annotation { "Feature Type Name" : "Feature", "Feature Type Description" : "" }
export const myFeature = defineFeature(function(context is Context, id is Id, definition is map)
    precondition{}
    {
        {
            var Q0;
            Q0=qCreatedBy(makeId("Top.planeOp"),FACE);
            var sketch = newSketch(context, id + "F0", { "sketchPlane" : qUnion([Q0])});
            skLineSegment(sketch, "E0.bottom", {"start": v(-25, 46.27) * mm, "end": v(25, 46.27) * mm});
            skLineSegment(sketch, "E0.top", {"start": v(-25, -46.27) * mm, "end": v(25, -46.27) * mm});
            skLineSegment(sketch, "E0.left", {"start": v(-25, 46.27) * mm, "end": v(-25, -46.27) * mm});
            skLineSegment(sketch, "E0.right", {"start": v(25, 46.27) * mm, "end": v(25, -46.27) * mm});
            skPoint(sketch, "E0.middle", {"position": v(0, 0) * mm});
            skCircle(sketch, "E1", {"center": v(0, 27.62) * mm, "radius": 4.09 * mm});
            skSolve(sketch);
        }
        {
            var Q0;
            Q0 = qSketchRegion(id + "F0", true);
            extrude(context, id + "F1", {"entities" : qUnion([Q0]), "depth" : 6.35 * mm, "offsetDistance" : 25.4 * mm});
        }
        {
            var Q0;
            Q0=makeQuery(id+"F1.opExtrude","CAP_FACE",FACE,{"disambiguationData":[OSD([sQuery(id+"F0.wireOp",EDGE,"E0.bottom"),sQuery(id+"F0.wireOp",EDGE,"E0.top"),sQuery(id+"F0.wireOp",EDGE,"E0.left"),sQuery(id+"F0.wireOp",EDGE,"E0.right"),sQuery(id+"F0.wireOp",EDGE,"E1")])],"isStart":false});
            var sketch = newSketch(context, id + "F2", { "sketchPlane" : qUnion([Q0])});
            skArc(sketch, "E2", {"start": v(0, 43.07) * mm, "mid": v(-15.22, 38.2) * mm, "end": v(-25, 25.58) * mm});
            skArc(sketch, "E3", {"start": v(-25, -29.22) * mm, "mid": v(-15.14, -41.63) * mm, "end": v(0, -46.27) * mm});
            skArc(sketch, "E4.MirrorCS", {"start": v(0, 43.07) * mm, "mid": v(15.22, 38.2) * mm, "end": v(25, 25.58) * mm});
            skArc(sketch, "E5.MirrorCS", {"start": v(25, -29.22) * mm, "mid": v(15.14, -41.63) * mm, "end": v(0, -46.27) * mm});
            skSolve(sketch);
        }
        {
            var Q0;
            {var subQ3=sQuery(id+"F2.wireOp",EDGE,"E2");Q0=makeQuery(id+"F2.imprint","IMPRINT",FACE,{"disambiguationData":[TD([[makeQuery(id+"F2.imprint","IMPRINT",EDGE,{"derivedFrom":subQ3}),-1.0]])]});}
            var Q1;
            {var subQ0=sQuery(id+"F2.wireOp",EDGE,"E3");var subQ1=makeQuery(id+"F1.opExtrude","CAP_EDGE",EDGE,{"disambiguationData":[OSD([sQuery(id+"F0.wireOp",EDGE,"E0.left")])],"isStart":false});var subQ2=makeQuery(id+"F2.imprint","INTERSECT",VERTEX,{"derivedFrom":[subQ1,subQ0]});Q1=makeQuery(id+"F2.imprint","IMPRINT",FACE,{"disambiguationData":[TD([[makeQuery(id+"F2.imprint","IMPRINT",EDGE,{"disambiguationData":[TD([[subQ2,-1.0]])],"derivedFrom":subQ0}),-1.0]])]});}
            var Q2;
            {var subQ0=sQuery(id+"F2.wireOp",EDGE,"E5.MirrorCS");var subQ1=makeQuery(id+"F1.opExtrude","CAP_EDGE",EDGE,{"disambiguationData":[OSD([sQuery(id+"F0.wireOp",EDGE,"E0.right")])],"isStart":false});var subQ2=makeQuery(id+"F2.imprint","INTERSECT",VERTEX,{"derivedFrom":[subQ1,subQ0]});Q2=makeQuery(id+"F2.imprint","IMPRINT",FACE,{"disambiguationData":[TD([[makeQuery(id+"F2.imprint","IMPRINT",EDGE,{"disambiguationData":[TD([[subQ2,-1.0]])],"derivedFrom":subQ0}),1.0]])]});}
            extrude(context, id + "F3", {"entities" : qUnion([Q0, Q1, Q2]), "operationType" : NewBodyOperationType.REMOVE, "endBound" : BoundingType.THROUGH_ALL, "oppositeDirection" : true, "depth" : 12.7 * mm, "offsetDistance" : 25.4 * mm});
        }
        {
            var Q0;
            Q0=makeQuery(id+"F1.opExtrude","CAP_FACE",FACE,{"disambiguationData":[OSD([sQuery(id+"F0.wireOp",EDGE,"E0.bottom"),sQuery(id+"F0.wireOp",EDGE,"E0.top"),sQuery(id+"F0.wireOp",EDGE,"E0.left"),sQuery(id+"F0.wireOp",EDGE,"E0.right"),sQuery(id+"F0.wireOp",EDGE,"E1")])],"isStart":false});
            var sketch = newSketch(context, id + "F4", { "sketchPlane" : qUnion([Q0])});
            skText(sketch, "E6", { "text": "Chichester Badgers", "fontName": "OpenSans-Bold.ttf"});
            const initialGuessF4  = {"E6": [-0.025, 0.00772, 1, 0, 0.00373]};
            skSetInitialGuess(sketch, initialGuessF4);
            skSolve(sketch);
        }
        {
            var Q0;
            Q0 = qSketchRegion(id + "F4", true);
            extrude(context, id + "F5", {"entities" : qUnion([Q0]), "operationType" : NewBodyOperationType.ADD, "depth" : 0.25 * mm, "offsetDistance" : 25.4 * mm});
        }
        {
            var Q0;
            {var subQ0=sQuery(id+"F0.wireOp",EDGE,"E1");var subQ1=sQuery(id+"F0.wireOp",EDGE,"E0.right");var subQ2=sQuery(id+"F0.wireOp",EDGE,"E0.left");var subQ3=sQuery(id+"F0.wireOp",EDGE,"E0.top");Q0=makeQuery(id+"F5.boolean.opBoolean","SPLIT",FACE,{"disambiguationData":[TD([makeQuery(id+"F1.opExtrude","SWEPT_FACE",FACE,{"disambiguationData":[OSD([subQ3])]})])],"derivedFrom":makeQuery(id+"F1.opExtrude","CAP_FACE",FACE,{"disambiguationData":[OSD([sQuery(id+"F0.wireOp",EDGE,"E0.bottom"),subQ3,subQ2,subQ1,subQ0])],"isStart":false})});}
            var sketch = newSketch(context, id + "F6", { "sketchPlane" : qUnion([Q0])});
            skPoint(sketch, "E7", {"position": v(-25, 15.62) * mm});
            skPoint(sketch, "E8", {"position": v(25, 15.62) * mm});
            skSolve(sketch);
        }
        {
            var Q0;
            Q0=makeQuery(id+"F6.imprint","IMPRINT",FACE,{"disambiguationData":[TD([[makeQuery(id+"F6.imprint","IMPRINT",EDGE,{"derivedFrom":makeQuery(id+"F1.opExtrude","CAP_EDGE",EDGE,{"disambiguationData":[OSD([sQuery(id+"F0.wireOp",EDGE,"E1")])],"isStart":false})}),-1.0]])]});
            var sketch = newSketch(context, id + "F7", { "sketchPlane" : qUnion([Q0])});
            skEllipse(sketch, "E9", {"center": v(0, -11.91) * mm, "majorRadius": 24.9 * mm, "minorRadius": 19.11 * mm, "majorAxis": v(1, 0)});
            skEllipse(sketch, "E10", {"center": v(0, -11.91) * mm, "majorRadius": 14.12 * mm, "minorRadius": 18.34 * mm, "majorAxis": v(0, -1)});
            skEllipticalArc(sketch, "E11", {});
            skLineSegment(sketch, "E12", {"start": v(-14.02, -17.14) * mm, "end": v(-15.85, -18.2) * mm});
            skPoint(sketch, "E13.orphan", {"position": v(-13.45, -20.24) * mm});
            skPoint(sketch, "E14.end.orphan", {"position": v(-13.45, -17.17) * mm});
            skLineSegment(sketch, "E15", {"start": v(-15.96, -18.86) * mm, "end": v(-17.59, -13.85) * mm});
            skArc(sketch, "E16", {"start": v(-16.31, -12.5) * mm, "mid": v(-17.12, -13.02) * mm, "end": v(-17.59, -13.85) * mm});
            skLineSegment(sketch, "E17", {"start": v(-16.31, -12.5) * mm, "end": v(6.68, -5.17) * mm});
            skLineSegment(sketch, "E18", {"start": v(6.68, -5.17) * mm, "end": v(13.26, -3.08) * mm});
            skLineSegment(sketch, "E19", {"start": v(-14.02, -17.14) * mm, "end": v(15, -8.1) * mm});
            skArc(sketch, "E20", {"start": v(15, -8.1) * mm, "mid": v(16.2, -7.1) * mm, "end": v(16.36, -5.54) * mm});
            skArc(sketch, "E21", {"start": v(14.38, -3.15) * mm, "mid": v(13.83, -3) * mm, "end": v(13.26, -3.08) * mm});
            skLineSegment(sketch, "E22", {"start": v(-12.14, -12.2) * mm, "end": v(-13.07, -15.03) * mm});
            skLineSegment(sketch, "E23", {"start": v(-11.66, -12.05) * mm, "end": v(-12.04, -13.28) * mm});
            skLineSegment(sketch, "E24", {"start": v(-12.14, -12.2) * mm, "end": v(-11.66, -12.05) * mm});
            skLineSegment(sketch, "E25", {"start": v(-12.14, -13.6) * mm, "end": v(-12.6, -15.1) * mm});
            skArc(sketch, "E26", {"start": v(-13.07, -15.03) * mm, "mid": v(-12.87, -15.28) * mm, "end": v(-12.6, -15.1) * mm});
            skArc(sketch, "E27", {"start": v(-10.56, -14.39) * mm, "mid": v(-10.42, -14.3) * mm, "end": v(-10.3, -14.17) * mm});
            skArc(sketch, "E28", {"start": v(-10.01, -13.44) * mm, "mid": v(-10.32, -13.08) * mm, "end": v(-10.79, -13.02) * mm});
            skArc(sketch, "E29", {"start": v(-10.3, -14.17) * mm, "mid": v(-10.09, -13.84) * mm, "end": v(-10.01, -13.44) * mm});
            skArc(sketch, "E30.trimOffspring", {"start": v(-10.79, -13.02) * mm, "mid": v(-10.91, -13.01) * mm, "end": v(-11.04, -13.03) * mm});
            skArc(sketch, "E31", {"start": v(-11.28, -14.8) * mm, "mid": v(-10.9, -14.64) * mm, "end": v(-10.56, -14.39) * mm});
            skArc(sketch, "E32", {"start": v(-11.84, -14.95) * mm, "mid": v(-11.55, -14.92) * mm, "end": v(-11.28, -14.8) * mm});
            skArc(sketch, "E33", {"start": v(-12.48, -14.75) * mm, "mid": v(-12.36, -14.9) * mm, "end": v(-12.18, -14.95) * mm});
            skLineSegment(sketch, "E34", {"start": v(-12.19, -14.95) * mm, "end": v(-11.84, -14.95) * mm});
            skArc(sketch, "E35", {"start": v(-12, -14.29) * mm, "mid": v(-12.24, -14.35) * mm, "end": v(-12.41, -14.52) * mm});
            skArc(sketch, "E36", {"start": v(-12, -14.29) * mm, "mid": v(-12.03, -14.4) * mm, "end": v(-12, -14.52) * mm});
            skArc(sketch, "E37", {"start": v(-12, -14.52) * mm, "mid": v(-11.2, -14.35) * mm, "end": v(-10.63, -13.76) * mm});
            skArc(sketch, "E38", {"start": v(-10.58, -13.45) * mm, "mid": v(-10.82, -13.4) * mm, "end": v(-11.06, -13.38) * mm});
            skArc(sketch, "E39", {"start": v(-11.06, -13.38) * mm, "mid": v(-11.62, -13.52) * mm, "end": v(-12.16, -13.7) * mm});
            skPoint(sketch, "E40.orphan", {"position": v(-12.15, -13.65) * mm});
            skArc(sketch, "E41", {"start": v(-10.63, -13.76) * mm, "mid": v(-10.57, -13.6) * mm, "end": v(-10.58, -13.45) * mm});
            skArc(sketch, "E42", {"start": v(-10.88, -11.63) * mm, "mid": v(-11.99, -11.96) * mm, "end": v(-12.88, -12.69) * mm});
            skArc(sketch, "E43", {"start": v(-10.56, -11.76) * mm, "mid": v(-10.7, -11.66) * mm, "end": v(-10.88, -11.63) * mm});
            skArc(sketch, "E44", {"start": v(-10.88, -12.39) * mm, "mid": v(-10.66, -12.1) * mm, "end": v(-10.56, -11.76) * mm});
            skArc(sketch, "E45", {"start": v(-12.04, -13.28) * mm, "mid": v(-11.43, -12.86) * mm, "end": v(-10.88, -12.39) * mm});
            skArc(sketch, "E46", {"start": v(-11.04, -13.03) * mm, "mid": v(-10.7, -12.78) * mm, "end": v(-10.44, -12.47) * mm});
            skArc(sketch, "E47", {"start": v(-10.44, -12.47) * mm, "mid": v(-10.18, -12.13) * mm, "end": v(-10.12, -11.71) * mm});
            skArc(sketch, "E48", {"start": v(-12.88, -12.69) * mm, "mid": v(-12.9, -12.8) * mm, "end": v(-12.8, -12.82) * mm});
            skArc(sketch, "E49", {"start": v(-13.39, -12.96) * mm, "mid": v(-13.06, -13.05) * mm, "end": v(-12.8, -12.82) * mm});
            skArc(sketch, "E50", {"start": v(-13.28, -12.45) * mm, "mid": v(-13.4, -12.69) * mm, "end": v(-13.39, -12.96) * mm});
            skArc(sketch, "E51", {"start": v(-10.92, -11.25) * mm, "mid": v(-12.2, -11.63) * mm, "end": v(-13.28, -12.45) * mm});
            skArc(sketch, "E52", {"start": v(-10.12, -11.71) * mm, "mid": v(-10.43, -11.32) * mm, "end": v(-10.92, -11.25) * mm});
            skLineSegment(sketch, "E53", {"start": v(-7.27, -10.58) * mm, "end": v(-7.58, -12.17) * mm});
            skLineSegment(sketch, "E54", {"start": v(-7.58, -12.17) * mm, "end": v(-8.53, -12.42) * mm});
            skLineSegment(sketch, "E55", {"start": v(-9.32, -14.29) * mm, "end": v(-8.82, -12.95) * mm});
            skLineSegment(sketch, "E56", {"start": v(-8.82, -12.95) * mm, "end": v(-7.68, -12.6) * mm});
            skLineSegment(sketch, "E57", {"start": v(-7.68, -12.6) * mm, "end": v(-7.92, -13.93) * mm});
            skArc(sketch, "E58", {"start": v(-7.27, -10.58) * mm, "mid": v(-7.97, -11.45) * mm, "end": v(-8.53, -12.42) * mm});
            skArc(sketch, "E59", {"start": v(-7.92, -13.93) * mm, "mid": v(-7.66, -13.84) * mm, "end": v(-7.42, -13.7) * mm});
            skArc(sketch, "E60", {"start": v(-9.76, -14.2) * mm, "mid": v(-9.56, -14.33) * mm, "end": v(-9.32, -14.29) * mm});
            skArc(sketch, "E61", {"start": v(-9.32, -13.04) * mm, "mid": v(-9.6, -13.59) * mm, "end": v(-9.76, -14.2) * mm});
            skPoint(sketch, "E62.end.orphan", {"position": v(-9.76, -13.23) * mm});
            skArc(sketch, "E63", {"start": v(-9.32, -13.04) * mm, "mid": v(-9.55, -13.12) * mm, "end": v(-9.76, -13.23) * mm});
            skArc(sketch, "E64", {"start": v(-9.99, -13.04) * mm, "mid": v(-9.96, -13.24) * mm, "end": v(-9.75, -13.26) * mm});
            skArc(sketch, "E65", {"start": v(-9.18, -12.68) * mm, "mid": v(-9.61, -12.79) * mm, "end": v(-9.99, -13.04) * mm});
            skArc(sketch, "E66", {"start": v(-7.3, -10.13) * mm, "mid": v(-8.38, -11.3) * mm, "end": v(-9.18, -12.68) * mm});
            skLineSegment(sketch, "E67", {"start": v(-7.3, -10.13) * mm, "end": v(-7.16, -10.13) * mm});
            skLineSegment(sketch, "E68", {"start": v(-7.16, -10.13) * mm, "end": v(-7.16, -9.96) * mm});
            skArc(sketch, "E69", {"start": v(-6.74, -10.04) * mm, "mid": v(-6.94, -9.93) * mm, "end": v(-7.16, -9.96) * mm});
            skArc(sketch, "E70", {"start": v(-7.42, -13.7) * mm, "mid": v(-7, -11.88) * mm, "end": v(-6.74, -10.04) * mm});
            skLineSegment(sketch, "E71", {"start": v(-4.95, -9.85) * mm, "end": v(-5.84, -12.23) * mm});
            skArc(sketch, "E72", {"start": v(-5.84, -12.23) * mm, "mid": v(-5.87, -12.3) * mm, "end": v(-5.89, -12.4) * mm});
            skArc(sketch, "E73", {"start": v(-5.89, -12.4) * mm, "mid": v(-5.93, -12.74) * mm, "end": v(-5.72, -13.02) * mm});
            skPoint(sketch, "E73.startSnap0", {"position": v(-5.89, -12.64) * mm});
            skArc(sketch, "E74", {"start": v(-4.46, -9.71) * mm, "mid": v(-4.71, -9.76) * mm, "end": v(-4.95, -9.85) * mm});
            skArc(sketch, "E75", {"start": v(-5.46, -12.62) * mm, "mid": v(-4.95, -11.17) * mm, "end": v(-4.46, -9.71) * mm});
            skArc(sketch, "E76", {"start": v(-5.46, -12.62) * mm, "mid": v(-5.26, -12.58) * mm, "end": v(-5.07, -12.52) * mm});
            skArc(sketch, "E77", {"start": v(-5.72, -13.02) * mm, "mid": v(-4.4, -12.61) * mm, "end": v(-3.3, -11.75) * mm});
            skArc(sketch, "E78", {"start": v(-5.07, -12.52) * mm, "mid": v(-3.82, -11.67) * mm, "end": v(-3.04, -10.37) * mm});
            skArc(sketch, "E79", {"start": v(-3.04, -10.37) * mm, "mid": v(-3.22, -9.75) * mm, "end": v(-3.83, -9.52) * mm});
            skPoint(sketch, "E80.end.orphan", {"position": v(-4.46, -9.56) * mm});
            skArc(sketch, "E81", {"start": v(-4.17, -9.55) * mm, "mid": v(-4.78, -9.7) * mm, "end": v(-5.33, -10) * mm});
            skArc(sketch, "E82", {"start": v(-5.33, -10) * mm, "mid": v(-5.62, -10.2) * mm, "end": v(-5.85, -10.48) * mm});
            skLineSegment(sketch, "E83", {"start": v(-5.85, -10.48) * mm, "end": v(-5.72, -10.48) * mm});
            skArc(sketch, "E84", {"start": v(-6.35, -10.8) * mm, "mid": v(-5.97, -10.78) * mm, "end": v(-5.72, -10.48) * mm});
            skArc(sketch, "E85", {"start": v(-5.48, -9.6) * mm, "mid": v(-5.73, -9.74) * mm, "end": v(-5.95, -9.92) * mm});
            skArc(sketch, "E86", {"start": v(-6.2, -10.17) * mm, "mid": v(-6.37, -10.47) * mm, "end": v(-6.35, -10.8) * mm});
            skLineSegment(sketch, "E87", {"start": v(-6.2, -10.17) * mm, "end": v(-5.95, -9.92) * mm});
            skPoint(sketch, "E88.orphan", {"position": v(-6.09, -10.08) * mm});
            skLineSegment(sketch, "E89", {"start": v(-4.21, -9.56) * mm, "end": v(-3.83, -9.52) * mm});
            skArc(sketch, "E90", {"start": v(-2.96, -9.27) * mm, "mid": v(-4.25, -9.19) * mm, "end": v(-5.48, -9.6) * mm});
            skArc(sketch, "E91", {"start": v(-3.3, -11.75) * mm, "mid": v(-2.91, -11.36) * mm, "end": v(-2.67, -10.88) * mm});
            skArc(sketch, "E92", {"start": v(-2.67, -10.88) * mm, "mid": v(-2.5, -10.02) * mm, "end": v(-2.96, -9.27) * mm});
            skLineSegment(sketch, "E93", {"start": v(0.7, -10.36) * mm, "end": v(-0.44, -11.83) * mm});
            skLineSegment(sketch, "E94", {"start": v(-0.44, -11.83) * mm, "end": v(-1.1, -12.92) * mm});
            skLineSegment(sketch, "E95", {"start": v(-0.16, -10.4) * mm, "end": v(-0.9, -11.75) * mm});
            skLineSegment(sketch, "E96", {"start": v(-0.9, -11.75) * mm, "end": v(-1.53, -12.62) * mm});
            skArc(sketch, "E97", {"start": v(-1.53, -12.62) * mm, "mid": v(-1.58, -12.7) * mm, "end": v(-1.59, -12.8) * mm});
            skArc(sketch, "E98", {"start": v(-1.59, -12.8) * mm, "mid": v(-1.57, -13.03) * mm, "end": v(-1.33, -13.05) * mm});
            skArc(sketch, "E99.trimOffspring", {"start": v(-1.33, -13.05) * mm, "mid": v(-1.2, -13.01) * mm, "end": v(-1.1, -12.92) * mm});
            skArc(sketch, "E100", {"start": v(0.7, -10.36) * mm, "mid": v(0.52, -10.37) * mm, "end": v(0.36, -10.43) * mm});
            skArc(sketch, "E101", {"start": v(0.36, -10.43) * mm, "mid": v(0.16, -10.68) * mm, "end": v(-0.03, -10.94) * mm});
            skLineSegment(sketch, "E102", {"start": v(-0.03, -10.94) * mm, "end": v(0.88, -9.02) * mm});
            skArc(sketch, "E103", {"start": v(0.88, -9.02) * mm, "mid": v(0.67, -9) * mm, "end": v(0.47, -9.04) * mm});
            skArc(sketch, "E104", {"start": v(-1.63, -11.77) * mm, "mid": v(-0.79, -11.2) * mm, "end": v(-0.16, -10.4) * mm});
            skArc(sketch, "E105", {"start": v(-0.58, -10.4) * mm, "mid": v(-0.02, -9.75) * mm, "end": v(0.47, -9.04) * mm});
            skArc(sketch, "E106", {"start": v(-1.63, -11.33) * mm, "mid": v(-1.03, -10.94) * mm, "end": v(-0.58, -10.4) * mm});
            skArc(sketch, "E107", {"start": v(-1.82, -10.98) * mm, "mid": v(-1.8, -11.2) * mm, "end": v(-1.63, -11.33) * mm});
            skLineSegment(sketch, "E108", {"start": v(-1.82, -10.98) * mm, "end": v(-1.79, -10.72) * mm});
            skArc(sketch, "E109", {"start": v(-0.93, -9.2) * mm, "mid": v(-1.45, -9.91) * mm, "end": v(-1.79, -10.72) * mm});
            skArc(sketch, "E110", {"start": v(-0.31, -8.55) * mm, "mid": v(-0.65, -8.85) * mm, "end": v(-0.93, -9.2) * mm});
            skArc(sketch, "E111", {"start": v(0.15, -8.18) * mm, "mid": v(-0.1, -8.34) * mm, "end": v(-0.31, -8.55) * mm});
            skArc(sketch, "E112", {"start": v(0.38, -8.05) * mm, "mid": v(0.26, -8.1) * mm, "end": v(0.15, -8.18) * mm});
            skArc(sketch, "E113", {"start": v(0.6, -7.95) * mm, "mid": v(0.57, -7.96) * mm, "end": v(0.54, -7.98) * mm});
            skArc(sketch, "E114", {"start": v(0.85, -8) * mm, "mid": v(0.83, -7.93) * mm, "end": v(0.75, -7.91) * mm});
            skLineSegment(sketch, "E115", {"start": v(0.75, -7.91) * mm, "end": v(0.6, -7.95) * mm});
            skLineSegment(sketch, "E116", {"start": v(0.38, -8.05) * mm, "end": v(0.54, -7.98) * mm});
            skArc(sketch, "E117", {"start": v(0, -8.92) * mm, "mid": v(0.5, -8.54) * mm, "end": v(0.85, -8) * mm});
            skArc(sketch, "E118", {"start": v(-0.1, -8.84) * mm, "mid": v(-0.07, -8.9) * mm, "end": v(0, -8.92) * mm});
            skArc(sketch, "E119", {"start": v(-0.1, -8.84) * mm, "mid": v(-0.27, -9.03) * mm, "end": v(-0.17, -9.26) * mm});
            skArc(sketch, "E120", {"start": v(-0.17, -9.26) * mm, "mid": v(0.18, -9.24) * mm, "end": v(0.47, -9.04) * mm});
            skArc(sketch, "E121", {"start": v(0.47, -9.04) * mm, "mid": v(0.96, -8.6) * mm, "end": v(1.3, -8.05) * mm});
            skArc(sketch, "E122", {"start": v(1.3, -8.05) * mm, "mid": v(1.14, -7.66) * mm, "end": v(0.72, -7.61) * mm});
            skArc(sketch, "E123", {"start": v(0.72, -7.61) * mm, "mid": v(-0.18, -7.98) * mm, "end": v(-0.93, -8.6) * mm});
            skArc(sketch, "E124", {"start": v(-0.93, -8.6) * mm, "mid": v(-1.4, -9.1) * mm, "end": v(-1.79, -9.68) * mm});
            skArc(sketch, "E125", {"start": v(-1.79, -9.68) * mm, "mid": v(-2.07, -10.22) * mm, "end": v(-2.26, -10.8) * mm});
            skPoint(sketch, "E126.orphan", {"position": v(-2.2, -10.8) * mm});
            skArc(sketch, "E127", {"start": v(-2.05, -11.7) * mm, "mid": v(-1.85, -11.77) * mm, "end": v(-1.63, -11.77) * mm});
            skArc(sketch, "E128", {"start": v(-2.26, -10.8) * mm, "mid": v(-2.26, -11.26) * mm, "end": v(-2.05, -11.7) * mm});
            skArc(sketch, "E129", {"start": v(2.9, -8.65) * mm, "mid": v(2.57, -8.95) * mm, "end": v(2.3, -9.3) * mm});
            skArc(sketch, "E130", {"start": v(2.3, -9.3) * mm, "mid": v(2.05, -9.66) * mm, "end": v(1.96, -10.1) * mm});
            skArc(sketch, "E131", {"start": v(2.36, -10.3) * mm, "mid": v(2.49, -10.27) * mm, "end": v(2.6, -10.2) * mm});
            skArc(sketch, "E132", {"start": v(1.96, -10.1) * mm, "mid": v(2.02, -10.26) * mm, "end": v(2.19, -10.32) * mm});
            skLineSegment(sketch, "E133", {"start": v(2.19, -10.32) * mm, "end": v(2.36, -10.3) * mm});
            skArc(sketch, "E134", {"start": v(2.6, -10.2) * mm, "mid": v(3.07, -9.89) * mm, "end": v(3.47, -9.48) * mm});
            skArc(sketch, "E135", {"start": v(3.8, -9.05) * mm, "mid": v(3.86, -8.82) * mm, "end": v(3.87, -8.58) * mm});
            skLineSegment(sketch, "E136", {"start": v(3.8, -9.05) * mm, "end": v(3.47, -9.48) * mm});
            skLineSegment(sketch, "E137", {"start": v(2.9, -8.65) * mm, "end": v(3.54, -8.32) * mm});
            skArc(sketch, "E138", {"start": v(4.18, -8.52) * mm, "mid": v(4.02, -8.52) * mm, "end": v(3.87, -8.58) * mm});
            skArc(sketch, "E139", {"start": v(3.54, -8.32) * mm, "mid": v(3.57, -8.16) * mm, "end": v(3.54, -8) * mm});
            skArc(sketch, "E140", {"start": v(4.33, -8.82) * mm, "mid": v(4.29, -8.65) * mm, "end": v(4.18, -8.52) * mm});
            skArc(sketch, "E141", {"start": v(3.87, -9.69) * mm, "mid": v(4.17, -9.3) * mm, "end": v(4.33, -8.82) * mm});
            skArc(sketch, "E142", {"start": v(2.7, -10.59) * mm, "mid": v(3.33, -10.2) * mm, "end": v(3.87, -9.69) * mm});
            skArc(sketch, "E143", {"start": v(1.5, -9.73) * mm, "mid": v(1.46, -10.24) * mm, "end": v(1.74, -10.66) * mm});
            skArc(sketch, "E144", {"start": v(1.74, -10.66) * mm, "mid": v(2.22, -10.7) * mm, "end": v(2.7, -10.59) * mm});
            skArc(sketch, "E145", {"start": v(2.24, -8.8) * mm, "mid": v(1.83, -9.23) * mm, "end": v(1.5, -9.73) * mm});
            skArc(sketch, "E146", {"start": v(3.54, -8) * mm, "mid": v(3.14, -8.03) * mm, "end": v(2.79, -8.23) * mm});
            skArc(sketch, "E147", {"start": v(1.6, -8) * mm, "mid": v(1.46, -8.4) * mm, "end": v(1.66, -8.76) * mm});
            skArc(sketch, "E148", {"start": v(1.66, -8.76) * mm, "mid": v(1.95, -8.81) * mm, "end": v(2.24, -8.8) * mm});
            skArc(sketch, "E149", {"start": v(2.18, -7.92) * mm, "mid": v(2.16, -7.94) * mm, "end": v(2.14, -7.97) * mm});
            skArc(sketch, "E150", {"start": v(2.14, -7.97) * mm, "mid": v(2, -8.14) * mm, "end": v(1.97, -8.36) * mm});
            skArc(sketch, "E151", {"start": v(1.97, -8.4) * mm, "mid": v(2.2, -8.43) * mm, "end": v(2.44, -8.4) * mm});
            skArc(sketch, "E152", {"start": v(1.97, -8.36) * mm, "mid": v(1.96, -8.38) * mm, "end": v(1.97, -8.4) * mm});
            skArc(sketch, "E153.trimOffspring", {"start": v(2.44, -8.4) * mm, "mid": v(2.51, -8.39) * mm, "end": v(2.58, -8.36) * mm});
            skLineSegment(sketch, "E154", {"start": v(2.58, -8.36) * mm, "end": v(2.79, -8.23) * mm});
            skArc(sketch, "E155", {"start": v(3.18, -7.25) * mm, "mid": v(2.64, -7.52) * mm, "end": v(2.18, -7.92) * mm});
            skArc(sketch, "E156", {"start": v(3.18, -7.25) * mm, "mid": v(3.17, -7.34) * mm, "end": v(3.18, -7.43) * mm});
            skArc(sketch, "E157", {"start": v(3.18, -7.43) * mm, "mid": v(3.65, -7.3) * mm, "end": v(4, -6.97) * mm});
            skArc(sketch, "E158", {"start": v(4, -6.97) * mm, "mid": v(3.8, -6.74) * mm, "end": v(3.49, -6.77) * mm});
            skArc(sketch, "E159", {"start": v(3.45, -6.77) * mm, "mid": v(2.4, -7.22) * mm, "end": v(1.6, -8) * mm});
            skLineSegment(sketch, "E160", {"start": v(3.45, -6.77) * mm, "end": v(3.49, -6.77) * mm});
            skArc(sketch, "E161", {"start": v(7.53, -5.98) * mm, "mid": v(6.23, -6.36) * mm, "end": v(5.2, -7.25) * mm});
            skArc(sketch, "E162", {"start": v(5.2, -7.25) * mm, "mid": v(5.31, -7.24) * mm, "end": v(5.42, -7.2) * mm});
            skArc(sketch, "E163", {"start": v(5.2, -7.5) * mm, "mid": v(5.34, -7.37) * mm, "end": v(5.42, -7.2) * mm});
            skArc(sketch, "E164", {"start": v(4.65, -7.25) * mm, "mid": v(4.83, -7.56) * mm, "end": v(5.2, -7.5) * mm});
            skArc(sketch, "E165", {"start": v(5.93, -6.12) * mm, "mid": v(5.2, -6.58) * mm, "end": v(4.65, -7.25) * mm});
            skArc(sketch, "E166", {"start": v(6.97, -5.7) * mm, "mid": v(6.44, -5.88) * mm, "end": v(5.93, -6.12) * mm});
            skArc(sketch, "E167", {"start": v(8.09, -5.7) * mm, "mid": v(7.53, -5.62) * mm, "end": v(6.97, -5.7) * mm});
            skArc(sketch, "E168", {"start": v(8.4, -6.12) * mm, "mid": v(8.28, -5.88) * mm, "end": v(8.09, -5.7) * mm});
            skArc(sketch, "E169", {"start": v(7.97, -6.96) * mm, "mid": v(8.26, -6.58) * mm, "end": v(8.4, -6.12) * mm});
            skArc(sketch, "E170", {"start": v(7.89, -6.06) * mm, "mid": v(7.71, -5.98) * mm, "end": v(7.53, -5.98) * mm});
            skArc(sketch, "E171", {"start": v(7.8, -6.41) * mm, "mid": v(7.89, -6.24) * mm, "end": v(7.89, -6.06) * mm});
            skArc(sketch, "E172", {"start": v(6.41, -7.6) * mm, "mid": v(7.2, -7.1) * mm, "end": v(7.8, -6.41) * mm});
            skLineSegment(sketch, "E173", {"start": v(6.41, -7.6) * mm, "end": v(6.9, -6.38) * mm});
            skArc(sketch, "E174", {"start": v(6.9, -6.38) * mm, "mid": v(6.7, -6.22) * mm, "end": v(6.47, -6.35) * mm});
            skLineSegment(sketch, "E175", {"start": v(6.47, -6.35) * mm, "end": v(5.32, -9.2) * mm});
            skArc(sketch, "E176", {"start": v(5.32, -9.2) * mm, "mid": v(5.3, -9.44) * mm, "end": v(5.44, -9.63) * mm});
            skArc(sketch, "E177", {"start": v(5.44, -9.63) * mm, "mid": v(5.63, -9.59) * mm, "end": v(5.8, -9.48) * mm});
            skLineSegment(sketch, "E178", {"start": v(5.8, -9.48) * mm, "end": v(6.25, -8.06) * mm});
            skLineSegment(sketch, "E179", {"start": v(6.25, -8.06) * mm, "end": v(7.49, -8.75) * mm});
            skArc(sketch, "E180", {"start": v(7.49, -8.75) * mm, "mid": v(7.9, -8.91) * mm, "end": v(8.36, -8.96) * mm});
            skArc(sketch, "E181", {"start": v(8.36, -8.96) * mm, "mid": v(8.56, -8.8) * mm, "end": v(8.67, -8.56) * mm});
            skLineSegment(sketch, "E182", {"start": v(6.8, -7.82) * mm, "end": v(8.01, -8.47) * mm});
            skArc(sketch, "E183", {"start": v(8.01, -8.47) * mm, "mid": v(8.33, -8.58) * mm, "end": v(8.67, -8.56) * mm});
            skArc(sketch, "E184", {"start": v(6.8, -7.82) * mm, "mid": v(7.42, -7.44) * mm, "end": v(7.97, -6.96) * mm});
            skArc(sketch, "E185", {"start": v(11.05, -4.8) * mm, "mid": v(10.1, -5.38) * mm, "end": v(9.39, -6.24) * mm});
            skArc(sketch, "E186", {"start": v(11.27, -6.36) * mm, "mid": v(10.93, -6.31) * mm, "end": v(10.58, -6.28) * mm});
            skArc(sketch, "E187", {"start": v(10.16, -6.33) * mm, "mid": v(10.37, -6.31) * mm, "end": v(10.58, -6.28) * mm});
            skArc(sketch, "E188", {"start": v(9.39, -6.24) * mm, "mid": v(9.5, -6.33) * mm, "end": v(9.64, -6.35) * mm});
            skLineSegment(sketch, "E189", {"start": v(9.64, -6.35) * mm, "end": v(10.16, -6.33) * mm});
            skFitSpline(sketch, "E190", {"points": [v(11.05, -4.8) * mm, v(11.05, -5.04) * mm, v(11.92, -4.65) * mm, v(11.94, -4.34) * mm, v(11.22, -4.33) * mm, v(10.07, -4.88) * mm, v(9.42, -5.36) * mm, v(9.02, -5.8) * mm, v(8.84, -6.14) * mm, v(8.8, -6.43) * mm, v(9.04, -6.75) * mm, v(9.68, -6.81) * mm, v(10.93, -6.74) * mm, v(11.18, -6.8) * mm, v(11.16, -7.03) * mm, v(10.75, -7.4) * mm, v(10.3, -7.72) * mm, v(9.83, -7.93) * mm, v(9.22, -8.04) * mm, v(9.02, -8) * mm, v(8.98, -7.9) * mm, v(8.82, -7.98) * mm, v(8.74, -8.12) * mm, v(8.7, -8.23) * mm, v(8.98, -8.5) * mm, v(10.35, -8.21) * mm, v(11.27, -7.64) * mm, v(11.64, -7.18) * mm, v(11.72, -7) * mm, v(11.76, -6.7) * mm, v(11.6, -6.5) * mm, v(11.27, -6.36) * mm], "startDerivative": vector(-4.33, -13.13) * mm, "endDerivative": vector(-12.82, 4.46) * mm});
            skFitSpline(sketch, "E191", {"points": [v(-16.65, -9.17) * mm, v(-16.5, -9.16) * mm, v(-16.02, -8.46) * mm, v(-16.08, -8.37) * mm, v(-16.4, -8.51) * mm, v(-17.02, -9.12) * mm, v(-17.52, -10.05) * mm, v(-17.63, -10.52) * mm, v(-17.57, -11.02) * mm, v(-17.35, -11.12) * mm, v(-16.87, -10.88) * mm, v(-16.39, -10.42) * mm, v(-15.94, -9.81) * mm, v(-15.88, -9.8) * mm, v(-15.81, -10.05) * mm, v(-15.85, -10.36) * mm, v(-16.13, -10.71) * mm, v(-16.57, -11.11) * mm, v(-17.17, -11.41) * mm, v(-17.47, -11.43) * mm, v(-17.74, -11.33) * mm, v(-17.93, -11.15) * mm, v(-18.05, -10.8) * mm, v(-18.02, -10.24) * mm, v(-17.9, -9.72) * mm, v(-17.4, -8.96) * mm, v(-16.89, -8.42) * mm, v(-16.35, -8.1) * mm, v(-15.93, -8) * mm, v(-15.7, -8.04) * mm, v(-15.55, -8.27) * mm, v(-15.75, -8.85) * mm, v(-16.08, -9.28) * mm, v(-16.34, -9.48) * mm, v(-16.61, -9.48) * mm, v(-16.65, -9.17) * mm]});
            skFitSpline(sketch, "E192", {"points": [v(-15.24, -7.92) * mm, v(-15.13, -7.85) * mm, v(-15.07, -7.98) * mm, v(-14.41, -7.66) * mm, v(-14.03, -7.26) * mm, v(-13.71, -7.27) * mm, v(-13.93, -8.08) * mm, v(-14.21, -8.84) * mm, v(-14.19, -8.87) * mm, v(-13.63, -8.68) * mm, v(-12.97, -8.47) * mm, v(-12.93, -8.45) * mm, v(-12.54, -7.23) * mm, v(-12.43, -6.9) * mm, v(-12.01, -6.76) * mm, v(-11.9, -6.8) * mm, v(-11.97, -7.07) * mm, v(-12.36, -8.22) * mm, v(-12.63, -9.17) * mm, v(-12.91, -10.1) * mm, v(-12.97, -10.15) * mm, v(-13.32, -10.22) * mm, v(-13.38, -10.16) * mm, v(-13.05, -8.92) * mm, v(-13.1, -8.9) * mm, v(-14.29, -9.26) * mm, v(-14.36, -9.3) * mm, v(-14.68, -10.46) * mm, v(-14.73, -10.66) * mm, v(-15.13, -10.73) * mm, v(-15.24, -10.65) * mm, v(-14.84, -9.47) * mm, v(-14.93, -9.5) * mm, v(-15.24, -9.52) * mm, v(-15.38, -9.27) * mm, v(-14.67, -9.06) * mm, v(-14.64, -9) * mm, v(-14.37, -8.1) * mm, v(-14.61, -8.26) * mm, v(-15, -8.38) * mm, v(-15.24, -8.4) * mm, v(-15.36, -8.28) * mm, v(-15.39, -8.1) * mm, v(-15.24, -7.92) * mm]});
            skFitSpline(sketch, "E193", {"points": [v(-11.3, -7.05) * mm, v(-11.82, -8.57) * mm, v(-12.14, -9.53) * mm, v(-12.1, -9.86) * mm, v(-11.71, -9.74) * mm, v(-11.57, -9.48) * mm, v(-11.22, -8.34) * mm, v(-10.85, -7.21) * mm, v(-10.54, -6.32) * mm, v(-10.58, -6.27) * mm, v(-10.97, -6.37) * mm, v(-11.02, -6.42) * mm, v(-11.3, -7.05) * mm]});
            skFitSpline(sketch, "E194", {"points": [v(-8.62, -6.1) * mm, v(-8.6, -6.21) * mm, v(-8.85, -6.6) * mm, v(-9.04, -6.8) * mm, v(-9.22, -6.86) * mm, v(-9.29, -6.98) * mm, v(-9.2, -7.16) * mm, v(-8.91, -7.17) * mm, v(-8.59, -6.9) * mm, v(-8.25, -6.39) * mm, v(-8.16, -6.02) * mm, v(-8.22, -5.8) * mm, v(-8.4, -5.72) * mm, v(-8.7, -5.71) * mm, v(-9.2, -5.94) * mm, v(-9.66, -6.26) * mm, v(-10.04, -6.7) * mm, v(-10.38, -7.21) * mm, v(-10.6, -7.72) * mm, v(-10.7, -8.37) * mm, v(-10.48, -9) * mm, v(-9.9, -9.14) * mm, v(-9.19, -8.88) * mm, v(-8.41, -7.96) * mm, v(-8.48, -7.5) * mm, v(-8.74, -7.81) * mm, v(-9.13, -8.3) * mm, v(-9.63, -8.73) * mm, v(-10.02, -8.78) * mm, v(-10.21, -8.4) * mm, v(-10.13, -7.68) * mm, v(-9.63, -6.85) * mm, v(-9.1, -6.32) * mm, v(-8.62, -6.1) * mm]});
            skFitSpline(sketch, "E195", {"points": [v(-7.75, -5.57) * mm, v(-7.92, -5.68) * mm, v(-7.98, -5.9) * mm, v(-7.73, -6.13) * mm, v(-6.9, -5.75) * mm, v(-6.99, -5.95) * mm, v(-7.27, -6.73) * mm, v(-7.38, -6.8) * mm, v(-7.97, -6.93) * mm, v(-7.92, -7.12) * mm, v(-7.73, -7.24) * mm, v(-7.43, -7.15) * mm, v(-7.75, -8) * mm, v(-7.75, -8.48) * mm, v(-7.38, -8.41) * mm, v(-7.18, -7.94) * mm, v(-6.94, -7.02) * mm, v(-6.81, -6.96) * mm, v(-5.66, -6.63) * mm, v(-5.66, -6.68) * mm, v(-5.96, -7.62) * mm, v(-5.99, -7.88) * mm, v(-5.93, -7.95) * mm, v(-5.69, -7.85) * mm, v(-5.49, -7.7) * mm, v(-5.3, -7.04) * mm, v(-5.04, -6.2) * mm, v(-4.7, -5.05) * mm, v(-4.5, -4.6) * mm, v(-4.52, -4.48) * mm, v(-4.7, -4.48) * mm, v(-4.93, -4.54) * mm, v(-5.04, -4.7) * mm, v(-5.49, -6.15) * mm, v(-5.55, -6.18) * mm, v(-6.37, -6.42) * mm, v(-6.78, -6.59) * mm, v(-6.76, -6.52) * mm, v(-6.28, -5.1) * mm, v(-6.33, -4.98) * mm, v(-6.43, -4.9) * mm, v(-6.65, -4.98) * mm, v(-6.88, -5.24) * mm, v(-7.34, -5.61) * mm, v(-7.63, -5.65) * mm, v(-7.75, -5.57) * mm]});
            skFitSpline(sketch, "E196", {"points": [v(-2.39, -5.43) * mm, v(-2.29, -5.37) * mm, v(-2.05, -5.4) * mm, v(-1.95, -5.73) * mm, v(-2.12, -6.12) * mm, v(-2.62, -6.74) * mm, v(-3.22, -7.13) * mm, v(-3.46, -7.23) * mm, v(-3.92, -7.28) * mm, v(-4.25, -7.16) * mm, v(-4.42, -6.85) * mm, v(-4.35, -6.32) * mm, v(-3.79, -5.65) * mm, v(-3.87, -5.65) * mm, v(-4.16, -5.6) * mm, v(-4.36, -5.45) * mm, v(-4.39, -5.08) * mm, v(-4.1, -4.62) * mm, v(-3.45, -4.14) * mm, v(-2.77, -3.85) * mm, v(-2.4, -3.82) * mm, v(-2.24, -4) * mm, v(-2.3, -4.15) * mm, v(-2.84, -4.44) * mm, v(-2.96, -4.43) * mm, v(-2.96, -4.3) * mm, v(-3.62, -4.68) * mm, v(-3.97, -5.13) * mm, v(-3.93, -5.26) * mm, v(-3.22, -5.1) * mm, v(-2.98, -4.96) * mm, v(-2.69, -4.9) * mm, v(-2.59, -5) * mm, v(-2.62, -5.15) * mm, v(-2.76, -5.33) * mm, v(-3.12, -5.47) * mm, v(-3.38, -5.7) * mm, v(-3.64, -5.98) * mm, v(-3.85, -6.3) * mm, v(-3.94, -6.5) * mm, v(-3.96, -6.78) * mm, v(-3.85, -6.93) * mm, v(-3.33, -6.78) * mm, v(-2.79, -6.3) * mm, v(-2.36, -5.73) * mm, v(-2.39, -5.43) * mm]});
            skFitSpline(sketch, "E197", {"points": [v(0.3, -3.24) * mm, v(0.25, -3.35) * mm, v(0.28, -3.48) * mm, v(1.01, -3.15) * mm, v(1.1, -3.03) * mm, v(1.05, -2.87) * mm, v(0.88, -2.8) * mm, v(0.56, -2.83) * mm, v(0.16, -2.96) * mm, v(-0.57, -3.34) * mm, v(-1.17, -3.77) * mm, v(-1.52, -4.3) * mm, v(-1.6, -4.47) * mm, v(-1.57, -4.73) * mm, v(-1.32, -4.98) * mm, v(-0.44, -4.98) * mm, v(0.28, -4.97) * mm, v(0.42, -5.04) * mm, v(0.36, -5.2) * mm, v(0.1, -5.43) * mm, v(-0.32, -5.76) * mm, v(-0.72, -5.94) * mm, v(-0.94, -6) * mm, v(-1.26, -6.04) * mm, v(-1.37, -6) * mm, v(-1.38, -5.9) * mm, v(-1.55, -5.98) * mm, v(-1.64, -6.2) * mm, v(-1.5, -6.44) * mm, v(-0.9, -6.43) * mm, v(-0.1, -6.14) * mm, v(0.5, -5.7) * mm, v(0.84, -5.34) * mm, v(0.92, -4.93) * mm, v(0.7, -4.67) * mm, v(0.33, -4.57) * mm, v(-0.24, -4.59) * mm, v(-1.01, -4.6) * mm, v(-1.1, -4.5) * mm, v(-1.07, -4.35) * mm, v(-0.74, -4) * mm, v(0.3, -3.24) * mm]});
            skFitSpline(sketch, "E198", {"points": [v(3.06, -2.7) * mm, v(2.8, -3.38) * mm, v(2.34, -4.73) * mm, v(2.16, -4.73) * mm, v(1.95, -5.15) * mm, v(2, -5.43) * mm, v(2.43, -5.43) * mm, v(2.79, -4.92) * mm, v(3.07, -4) * mm, v(3.34, -3.15) * mm, v(3.49, -2.45) * mm, v(3.59, -2.38) * mm, v(4, -2.19) * mm, v(4.27, -1.95) * mm, v(4.31, -1.85) * mm, v(4.3, -1.76) * mm, v(4.23, -1.71) * mm, v(4.12, -1.68) * mm, v(4, -1.7) * mm, v(3.84, -1.76) * mm, v(3.68, -1.89) * mm, v(3.49, -2.07) * mm, v(3.4, -2.15) * mm, v(3.04, -2.33) * mm, v(2.6, -2.52) * mm, v(2.11, -2.7) * mm, v(1.78, -2.77) * mm, v(1.7, -2.75) * mm, v(1.7, -2.67) * mm, v(1.64, -2.63) * mm, v(1.48, -2.7) * mm, v(1.33, -2.9) * mm, v(1.38, -3.1) * mm, v(1.62, -3.24) * mm, v(2.31, -3.03) * mm, v(2.92, -2.74) * mm, v(3.09, -2.65) * mm, v(3.06, -2.7) * mm]});
            skFitSpline(sketch, "E199", {"points": [v(5.56, -1.66) * mm, v(5.21, -1.79) * mm, v(4.78, -2.2) * mm, v(4.57, -2.48) * mm, v(4.59, -2.64) * mm, v(4.83, -2.6) * mm, v(5.24, -2.48) * mm, v(5.4, -2.37) * mm, v(5.8, -2.27) * mm, v(5.92, -2.33) * mm, v(5.92, -2.5) * mm, v(5.75, -2.7) * mm, v(5.44, -2.81) * mm, v(5.3, -2.93) * mm, v(5.18, -3) * mm, v(5.01, -3.18) * mm, v(4.68, -3.61) * mm, v(4.56, -3.85) * mm, v(4.57, -4.12) * mm, v(4.59, -4.26) * mm, v(4.81, -4.3) * mm, v(5.08, -4.21) * mm, v(5.47, -3.93) * mm, v(5.77, -3.64) * mm, v(6.08, -3.21) * mm, v(6.16, -3.03) * mm, v(6.1, -2.81) * mm, v(6.3, -2.76) * mm, v(6.43, -2.74) * mm, v(6.55, -2.92) * mm, v(6.53, -3.2) * mm, v(6.43, -3.4) * mm, v(5.92, -4.04) * mm, v(5.46, -4.4) * mm, v(5.19, -4.56) * mm, v(4.98, -4.62) * mm, v(4.72, -4.64) * mm, v(4.48, -4.59) * mm, v(4.23, -4.44) * mm, v(4.1, -4.2) * mm, v(4.14, -3.8) * mm, v(4.72, -3.03) * mm, v(4.75, -3) * mm, v(4.73, -2.98) * mm, v(4.52, -2.99) * mm, v(4.33, -2.96) * mm, v(4.18, -2.83) * mm, v(4.1, -2.66) * mm, v(4.14, -2.4) * mm, v(4.3, -2.07) * mm, v(4.62, -1.76) * mm, v(4.93, -1.56) * mm, v(5.29, -1.37) * mm, v(5.67, -1.24) * mm, v(5.96, -1.17) * mm, v(6.22, -1.27) * mm, v(6.25, -1.48) * mm, v(5.95, -1.7) * mm, v(5.7, -1.76) * mm, v(5.56, -1.8) * mm, v(5.55, -1.72) * mm, v(5.56, -1.66) * mm]});
            skFitSpline(sketch, "E200", {"points": [v(7.34, -1.53) * mm, v(7.3, -1.63) * mm, v(7.4, -1.62) * mm, v(7.49, -1.6) * mm, v(7.45, -1.72) * mm, v(7.34, -1.84) * mm, v(7.18, -1.91) * mm, v(7, -1.92) * mm, v(6.87, -1.87) * mm, v(6.8, -1.72) * mm, v(6.88, -1.49) * mm, v(7.06, -1.27) * mm, v(7.38, -0.98) * mm, v(7.78, -0.73) * mm, v(8.09, -0.56) * mm, v(8.45, -0.4) * mm, v(9.13, -0.26) * mm, v(9.48, -0.26) * mm, v(9.8, -0.38) * mm, v(9.95, -0.62) * mm, v(9.95, -0.9) * mm, v(9.73, -1.32) * mm, v(9.3, -1.7) * mm, v(8.9, -2) * mm, v(8.65, -2.15) * mm, v(8.73, -2.24) * mm, v(9.36, -2.55) * mm, v(9.8, -2.77) * mm, v(10, -2.83) * mm, v(10.21, -2.82) * mm, v(10.24, -2.85) * mm, v(10.07, -3.15) * mm, v(9.92, -3.2) * mm, v(9.64, -3.15) * mm, v(9.28, -3.03) * mm, v(8.8, -2.74) * mm, v(8.27, -2.4) * mm, v(8.2, -2.37) * mm, v(8.11, -2.69) * mm, v(7.97, -3.15) * mm, v(7.88, -3.49) * mm, v(7.72, -3.65) * mm, v(7.5, -3.71) * mm, v(7.4, -3.73) * mm, v(7.39, -3.48) * mm, v(7.52, -3.03) * mm, v(7.78, -2.25) * mm, v(8.1, -1.4) * mm, v(8.25, -0.99) * mm, v(8.43, -0.82) * mm, v(8.65, -0.83) * mm, v(8.7, -1) * mm, v(8.64, -1.18) * mm, v(8.34, -1.95) * mm, v(8.43, -1.88) * mm, v(8.76, -1.7) * mm, v(9.3, -1.18) * mm, v(9.5, -0.78) * mm, v(9.5, -0.65) * mm, v(9.39, -0.56) * mm, v(9.13, -0.57) * mm, v(8.7, -0.67) * mm, v(8.31, -0.8) * mm, v(7.9, -1.06) * mm, v(7.52, -1.35) * mm, v(7.34, -1.53) * mm]});
            skFitSpline(sketch, "E201", {"points": [v(-5.73, -16.38) * mm, v(-5.88, -17.38) * mm, v(-4.46, -19.86) * mm, v(-1.67, -21.81) * mm, v(2.71, -23.03) * mm, v(5.5, -23.3) * mm, v(9.46, -22.6) * mm, v(13.26, -21.13) * mm, v(15, -19.57) * mm, v(15.75, -18.64) * mm, v(16.22, -17.58) * mm, v(16.37, -16.02) * mm, v(15.89, -14.63) * mm, v(15.97, -14.3) * mm, v(15.89, -14.07) * mm, v(15.75, -13.9) * mm, v(15.54, -13.87) * mm, v(15.56, -13.7) * mm, v(15.51, -13.48) * mm, v(15.35, -13.34) * mm, v(15.2, -13.27) * mm, v(15.04, -13.3) * mm, v(14.54, -13.03) * mm, v(13.7, -12.4) * mm, v(13.2, -12.05) * mm, v(12.2, -11.52) * mm, v(11.18, -11.14) * mm, v(10.4, -10.89) * mm, v(9.02, -10.58) * mm, v(7.84, -10.32) * mm, v(7.84, -10.32) * mm], "startDerivative": vector(-10.21, -27.02) * mm, "endDerivative": vector(-0.32, -0.3) * mm});
            skFitSpline(sketch, "E202", {"points": [v(-5.73, -16.38) * mm, v(-4.22, -14.84) * mm, v(-3.58, -13.88) * mm, v(-3.56, -13.88) * mm, v(-3.5, -13.86) * mm], "startDerivative": vector(3.23, 2.87) * mm, "endDerivative": vector(0.8, 0.3) * mm});
            skLineSegment(sketch, "E203", {"start": v(0, 2.2) * mm, "end": v(0, -26.03) * mm});
            const initialGuessF7  = {"E11": [-0.013453744351863861, -0.0187006127089262, 1, 0, 0.0025196997448801994, 0.0016045304282647102, 2.8303313143950946, 1.797063792498224]};
            skSetInitialGuess(sketch, initialGuessF7);
            skSolve(sketch);
        }
        {
            var Q0;
            Q0 = qSketchRegion(id + "F7", true);
            extrude(context, id + "F8", {"entities" : qUnion([Q0]), "operationType" : NewBodyOperationType.REMOVE, "oppositeDirection" : true, "depth" : 1.27 * mm, "offsetDistance" : 25.4 * mm});
        }
    });